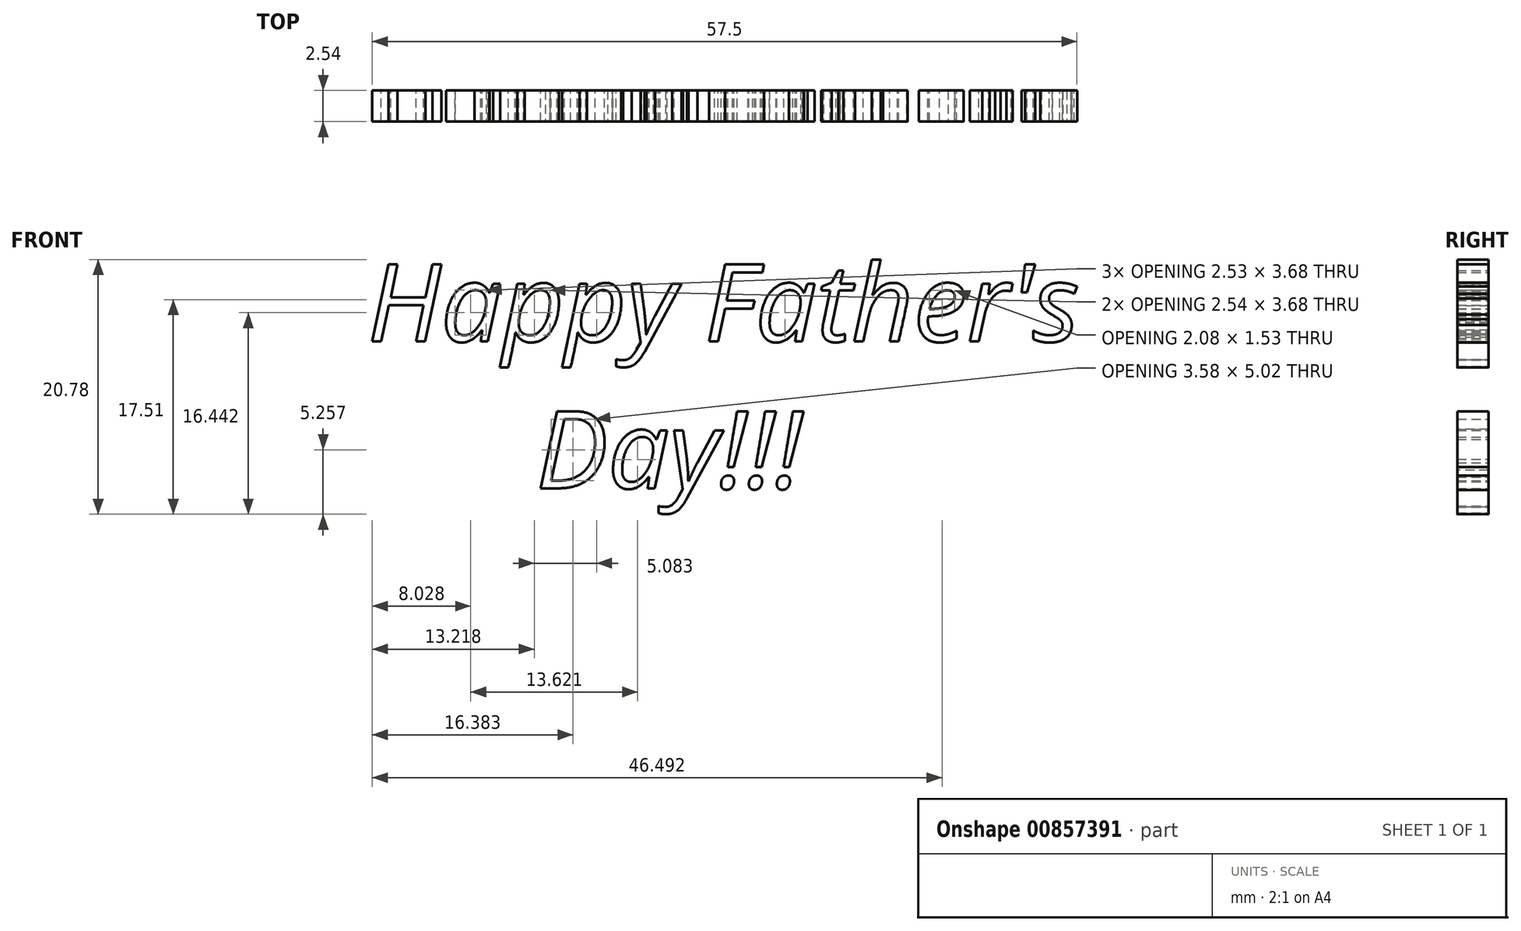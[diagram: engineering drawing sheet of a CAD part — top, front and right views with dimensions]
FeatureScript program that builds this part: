
annotation { "Feature Type Name" : "Feature", "Feature Type Description" : "" }
export const myFeature = defineFeature(function(context is Context, id is Id, definition is map)
    precondition{}
    {
        {
            var Q0;
            Q0=qCreatedBy(makeId("Front.planeOp"),FACE);
            var sketch = newSketch(context, id + "F0", { "sketchPlane" : qUnion([Q0])});
            skText(sketch, "E0", { "text": "Happy Father\'s\n      Day!!!", "fontName": "OpenSans-Italic.ttf"});
            const initialGuessF0  = {"E0": [0.01201, 0, 1, 0, 0.00634]};
            skSetInitialGuess(sketch, initialGuessF0);
            skSolve(sketch);
        }
        {
            var Q0;
            Q0 = qSketchRegion(id + "F0", true);
            extrude(context, id + "F1", {"entities" : qUnion([Q0]), "depth" : 2.54 * mm, "offsetDistance" : 25.4 * mm});
        }
    });
